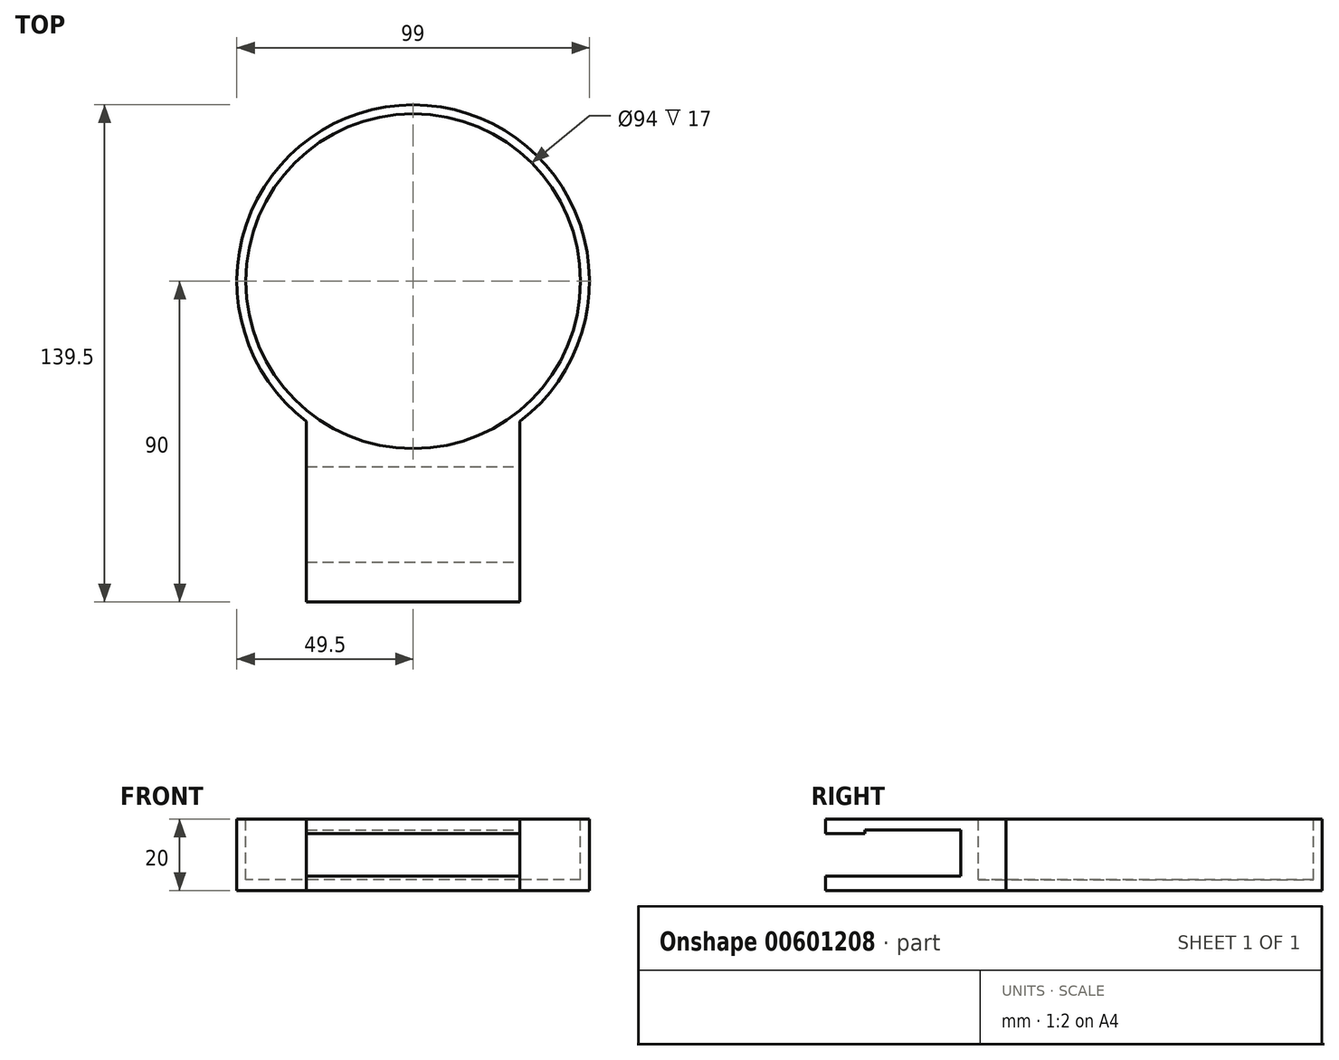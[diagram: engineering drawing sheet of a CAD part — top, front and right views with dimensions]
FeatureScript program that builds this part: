
annotation { "Feature Type Name" : "Feature", "Feature Type Description" : "" }
export const myFeature = defineFeature(function(context is Context, id is Id, definition is map)
    precondition{}
    {
        {
            var Q0;
            Q0=qCreatedBy(makeId("Top.planeOp"),FACE);
            var sketch = newSketch(context, id + "F0", { "sketchPlane" : qUnion([Q0])});
            skLineSegment(sketch, "E0.bottom", {"start": v(0, 0) * mm, "end": v(60, 0) * mm});
            skLineSegment(sketch, "E0.top", {"start": v(0, 90) * mm, "end": v(60, 90) * mm});
            skLineSegment(sketch, "E0.left", {"start": v(0, 0) * mm, "end": v(0, 90) * mm});
            skLineSegment(sketch, "E0.right", {"start": v(60, 0) * mm, "end": v(60, 90) * mm});
            skSolve(sketch);
        }
        {
            var Q0;
            Q0 = qSketchRegion(id + "F0", true);
            extrude(context, id + "F1", {"entities" : qUnion([Q0]), "depth" : 20 * mm, "offsetDistance" : 25 * mm});
        }
        {
            var Q0;
            Q0=qCreatedBy(makeId("Top.planeOp"),FACE);
            var sketch = newSketch(context, id + "F2", { "sketchPlane" : qUnion([Q0])});
            skLineSegment(sketch, "E1.0", {"start": v(0, 90) * mm, "end": v(60, 90) * mm});
            skCircle(sketch, "E2", {"center": v(30, 90) * mm, "radius": 49.5 * mm});
            skSolve(sketch);
        }
        {
            var Q0;
            Q0 = qSketchRegion(id + "F2", true);
            extrude(context, id + "F3", {"entities" : qUnion([Q0]), "operationType" : NewBodyOperationType.ADD, "depth" : 20 * mm, "offsetDistance" : 25 * mm});
        }
        {
            var Q0;
            Q0=makeQuery(id+"F3.boolean.opBoolean","MERGE",FACE,{"derivedFrom":[makeQuery(id+"F1.opExtrude","CAP_FACE",FACE,{"disambiguationData":[OSD([sQuery(id+"F0.wireOp",EDGE,"E0.bottom"),sQuery(id+"F0.wireOp",EDGE,"E0.top"),sQuery(id+"F0.wireOp",EDGE,"E0.left"),sQuery(id+"F0.wireOp",EDGE,"E0.right")])],"isStart":false}),makeQuery(id+"F3.opExtrude","CAP_FACE",FACE,{"disambiguationData":[OSD([sQuery(id+"F2.wireOp",EDGE,"E2")])],"isStart":false})]});
            var sketch = newSketch(context, id + "F4", { "sketchPlane" : qUnion([Q0])});
            skArc(sketch, "E3.0", {"start": v(60, 50.63) * mm, "mid": v(30, 139.5) * mm, "end": v(0, 50.63) * mm, "construction": true});
            skCircle(sketch, "E4", {"center": v(30, 90) * mm, "radius": 47 * mm});
            skSolve(sketch);
        }
        {
            var Q0;
            Q0 = qSketchRegion(id + "F4", true);
            extrude(context, id + "F5", {"entities" : qUnion([Q0]), "operationType" : NewBodyOperationType.REMOVE, "oppositeDirection" : true, "depth" : 17 * mm, "offsetDistance" : 25 * mm});
        }
        {
            var Q0;
            Q0=makeQuery(id+"F3.boolean.opBoolean","MERGE",FACE,{"derivedFrom":[makeQuery(id+"F1.opExtrude","CAP_FACE",FACE,{"disambiguationData":[OSD([sQuery(id+"F0.wireOp",EDGE,"E0.bottom"),sQuery(id+"F0.wireOp",EDGE,"E0.top"),sQuery(id+"F0.wireOp",EDGE,"E0.left"),sQuery(id+"F0.wireOp",EDGE,"E0.right")])],"isStart":false}),makeQuery(id+"F3.opExtrude","CAP_FACE",FACE,{"disambiguationData":[OSD([sQuery(id+"F2.wireOp",EDGE,"E2")])],"isStart":false})]});
            var sketch = newSketch(context, id + "F6", { "sketchPlane" : qUnion([Q0])});
            skLineSegment(sketch, "E5", {"start": v(30, 0) * mm, "end": v(30, 43) * mm, "construction": true});
            skLineSegment(sketch, "E6", {"start": v(30, 43) * mm, "end": v(60, 43) * mm, "construction": true});
            skSolve(sketch);
        }
        {
            var Q0;
            Q0=makeQuery(id+"F1.opExtrude","SWEPT_FACE",FACE,{"disambiguationData":[OSD([sQuery(id+"F0.wireOp",EDGE,"E0.right")])]});
            var sketch = newSketch(context, id + "F7", { "sketchPlane" : qUnion([Q0])});
            skLineSegment(sketch, "E7.0.0", {"start": v(50.63, 0) * mm, "end": v(50.63, 20) * mm});
            skLineSegment(sketch, "E7.0.1", {"start": v(50.63, 20) * mm, "end": v(0, 20) * mm});
            skLineSegment(sketch, "E7.0.2", {"start": v(0, 20) * mm, "end": v(0, 0) * mm});
            skLineSegment(sketch, "E7.0.3", {"start": v(0, 0) * mm, "end": v(50.63, 0) * mm, "construction": true});
            skPoint(sketch, "E8.0", {"position": v(43, 20) * mm});
            skLineSegment(sketch, "E9", {"start": v(43, 20) * mm, "end": v(38, 20) * mm, "construction": true});
            skLineSegment(sketch, "E10", {"start": v(38, 20) * mm, "end": v(38, 0) * mm, "construction": true});
            skLineSegment(sketch, "E11.bottom", {"start": v(38, 16) * mm, "end": v(0, 16) * mm, "construction": true});
            skLineSegment(sketch, "E11.top", {"start": v(38, 4) * mm, "end": v(0, 4) * mm, "construction": true});
            skLineSegment(sketch, "E11.left", {"start": v(38, 16) * mm, "end": v(38, 4) * mm, "construction": true});
            skLineSegment(sketch, "E11.right", {"start": v(0, 16) * mm, "end": v(0, 4) * mm, "construction": true});
            skLineSegment(sketch, "E12", {"start": v(20.42, 0) * mm, "end": v(20.42, 4) * mm, "construction": true});
            skLineSegment(sketch, "E13", {"start": v(17.38, 0) * mm, "end": v(17.38, 4) * mm, "construction": true});
            skLineSegment(sketch, "E14", {"start": v(17.38, 4) * mm, "end": v(38, 4) * mm});
            skLineSegment(sketch, "E15", {"start": v(17.38, 4) * mm, "end": v(0, 4) * mm});
            skLineSegment(sketch, "E16", {"start": v(38, 20) * mm, "end": v(38, 17) * mm, "construction": true});
            skLineSegment(sketch, "E17", {"start": v(38, 17) * mm, "end": v(11.12, 17) * mm});
            skLineSegment(sketch, "E18", {"start": v(11.12, 17) * mm, "end": v(11.12, 16) * mm});
            skLineSegment(sketch, "E19", {"start": v(11.12, 16) * mm, "end": v(0, 16) * mm});
            skLineSegment(sketch, "E20", {"start": v(38, 17) * mm, "end": v(38, 16) * mm});
            skLineSegment(sketch, "E21", {"start": v(0, 16) * mm, "end": v(0, 4) * mm});
            skLineSegment(sketch, "E22", {"start": v(38, 16) * mm, "end": v(38, 4) * mm});
            skSolve(sketch);
        }
        {
            var Q0;
            Q0 = qSketchRegion(id + "F7", true);
            extrude(context, id + "F8", {"entities" : qUnion([Q0]), "operationType" : NewBodyOperationType.REMOVE, "endBound" : BoundingType.THROUGH_ALL, "oppositeDirection" : true, "depth" : 25 * mm, "offsetDistance" : 25 * mm});
        }
    });
